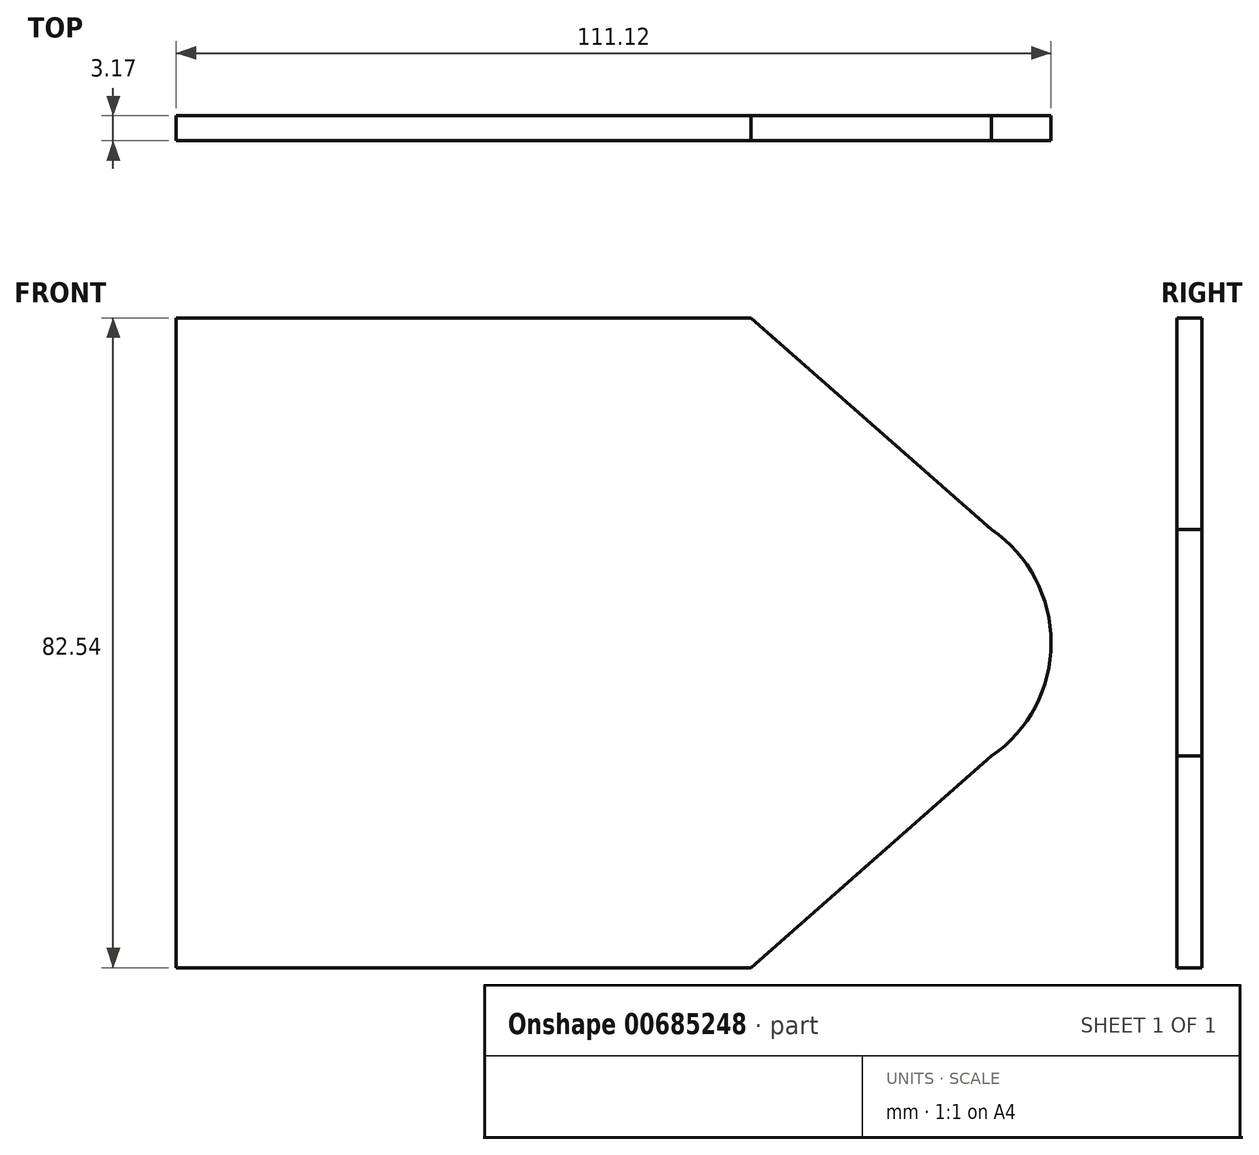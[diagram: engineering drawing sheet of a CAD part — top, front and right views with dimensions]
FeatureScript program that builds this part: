
annotation { "Feature Type Name" : "Feature", "Feature Type Description" : "" }
export const myFeature = defineFeature(function(context is Context, id is Id, definition is map)
    precondition{}
    {
        {
            var Q0;
            Q0=qCreatedBy(makeId("Front.planeOp"),FACE);
            var sketch = newSketch(context, id + "F0", { "sketchPlane" : qUnion([Q0])});
            skLineSegment(sketch, "E0.bottom", {"start": v(17.46, 41.28) * mm, "end": v(-55.56, 41.28) * mm});
            skLineSegment(sketch, "E0.right", {"start": v(-55.56, 41.28) * mm, "end": v(-55.56, -41.28) * mm});
            skPoint(sketch, "E0.middle", {"position": v(0, 0) * mm});
            skArc(sketch, "E1", {"start": v(48, -14.4) * mm, "mid": v(55.56, 0) * mm, "end": v(48, 14.4) * mm});
            skLineSegment(sketch, "E2", {"start": v(48, 14.4) * mm, "end": v(17.46, 41.28) * mm});
            skLineSegment(sketch, "E3", {"start": v(48, -14.4) * mm, "end": v(17.46, -41.28) * mm});
            skPoint(sketch, "E4.orphan", {"position": v(55.56, 41.28) * mm});
            skLineSegment(sketch, "E5", {"start": v(-55.56, -41.28) * mm, "end": v(17.46, -41.28) * mm});
            skPoint(sketch, "E0.left.end.orphan", {"position": v(55.56, -41.28) * mm});
            skSolve(sketch);
        }
        {
            var Q0;
            Q0 = qSketchRegion(id + "F0", true);
            extrude(context, id + "F1", {"entities" : qUnion([Q0]), "depth" : 3.17 * mm, "offsetDistance" : 25.4 * mm});
        }
    });
